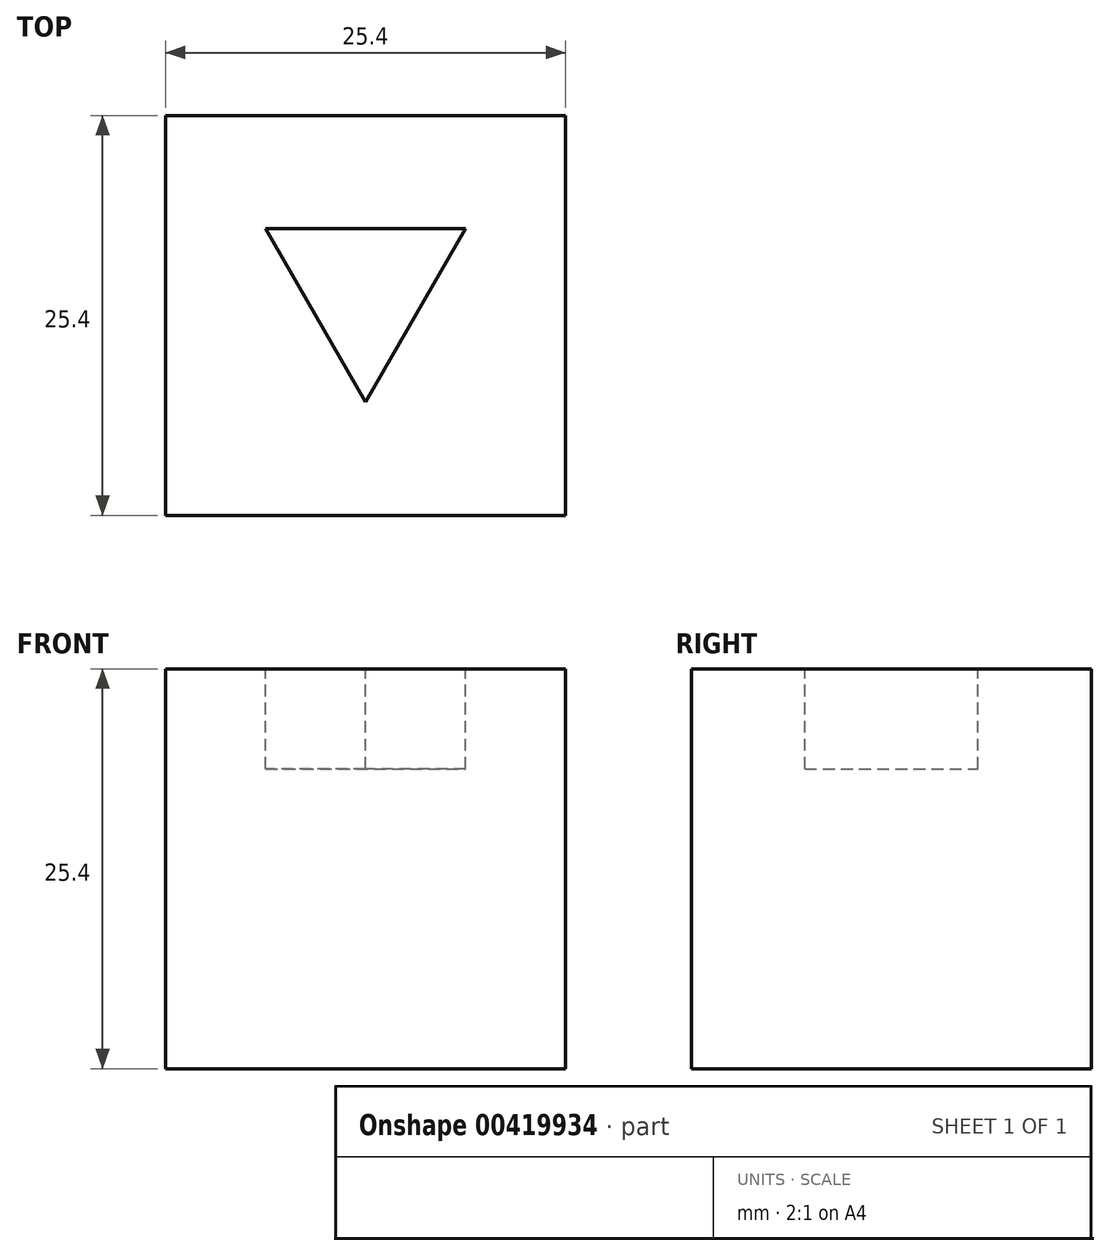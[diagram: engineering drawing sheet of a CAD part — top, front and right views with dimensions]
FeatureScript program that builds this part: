
annotation { "Feature Type Name" : "Feature", "Feature Type Description" : "" }
export const myFeature = defineFeature(function(context is Context, id is Id, definition is map)
    precondition{}
    {
        {
            var Q0;
            Q0=qCreatedBy(makeId("Top.planeOp"),FACE);
            var sketch = newSketch(context, id + "F0", { "sketchPlane" : qUnion([Q0])});
            skLineSegment(sketch, "E0.bottom", {"start": v(0, 0) * mm, "end": v(25.4, 0) * mm});
            skLineSegment(sketch, "E0.top", {"start": v(0, 25.4) * mm, "end": v(25.4, 25.4) * mm});
            skLineSegment(sketch, "E0.left", {"start": v(0, 0) * mm, "end": v(0, 25.4) * mm});
            skLineSegment(sketch, "E0.right", {"start": v(25.4, 0) * mm, "end": v(25.4, 25.4) * mm});
            skSolve(sketch);
        }
        {
            var Q0;
            Q0=makeQuery(id+"F0.imprint","IMPRINT",FACE,{"disambiguationData":[TD([[makeQuery(id+"F0.imprint","IMPRINT",EDGE,{"derivedFrom":sQuery(id+"F0.wireOp",EDGE,"E0.bottom")}),1.0]])]});
            extrude(context, id + "F1", {"entities" : qUnion([Q0]), "depth" : 25.4 * mm});
        }
        {
            var Q0;
            Q0=makeQuery(id+"F1.opExtrude","CAP_FACE",FACE,{"disambiguationData":[OSD([sQuery(id+"F0.wireOp",EDGE,"E0.bottom"),sQuery(id+"F0.wireOp",EDGE,"E0.top"),sQuery(id+"F0.wireOp",EDGE,"E0.left"),sQuery(id+"F0.wireOp",EDGE,"E0.right")])],"isStart":false});
            var sketch = newSketch(context, id + "F2", { "sketchPlane" : qUnion([Q0])});
            skLineSegment(sketch, "E1", {"start": v(6.35, 18.2) * mm, "end": v(19.05, 18.2) * mm});
            skLineSegment(sketch, "E2", {"start": v(19.05, 18.2) * mm, "end": v(12.7, 7.2) * mm});
            skLineSegment(sketch, "E3", {"start": v(12.7, 7.2) * mm, "end": v(6.35, 18.2) * mm});
            skLineSegment(sketch, "E4", {"start": v(12.7, 18.2) * mm, "end": v(12.7, 25.4) * mm, "construction": true});
            skLineSegment(sketch, "E5", {"start": v(12.7, 7.2) * mm, "end": v(12.7, 0) * mm, "construction": true});
            skLineSegment(sketch, "E6", {"start": v(6.35, 18.2) * mm, "end": v(0, 18.2) * mm, "construction": true});
            skLineSegment(sketch, "E7", {"start": v(19.05, 18.2) * mm, "end": v(25.4, 18.2) * mm, "construction": true});
            skSolve(sketch);
        }
        {
            var Q0;
            Q0=makeQuery(id+"F2.imprint","IMPRINT",FACE,{"disambiguationData":[TD([[makeQuery(id+"F2.imprint","IMPRINT",EDGE,{"derivedFrom":sQuery(id+"F2.wireOp",EDGE,"E1")}),-1.0]])]});
            extrude(context, id + "F3", {"entities" : qUnion([Q0]), "operationType" : NewBodyOperationType.REMOVE, "oppositeDirection" : true, "depth" : 6.35 * mm});
        }
    });
